# Revit family: Seating-Stool-Teknion-Zones_ZNMT_High_Backless-R2013
name_source: partatom
category: Furniture
revit_build: Autodesk Revit Architecture 2013 (Build: 20130531_2115(x64)
units: mm (PartAtom-declared; Revit-internal decimal feet)

## types (2) — shared parameters
Assembly Code = E2020200
Depth = 16 15/32"
Manufacturer = Teknion
Manufacturer Fax = 416.661.4586
Part Number = ZNMT
Product Documentation Link = http://www.teknion.com
Product Line = Zones
Product Page URL = http://www.teknion.com
Series = Zones
Sustainability Data = http://www.teknion.com
URL = www.teknion.com
Warranty = http://www.teknion.com
Width = 16 15/32"

## per-type parameters (varying)
| type | Description | Footrest Height | Height | Legs Bar Height | Legs Counter Height | Model |
| Bar Seat Height | Zones High Backless Stool, 4-Wood Legs, Uph, Bar Height | 13 5/32" | 30 3/4" | Yes | No | ZNMTUB |
| Counter Seat Height | Zones High Backless Stool, 4-Wood Legs, Uph, Counter Height | 7 3/16" | 24 1/4" | No | Yes | ZNMTUC |

## geometry (parser evidence)
native form markers: Blend x55, Sweep x4
no freeform markers — native parametric forms only
